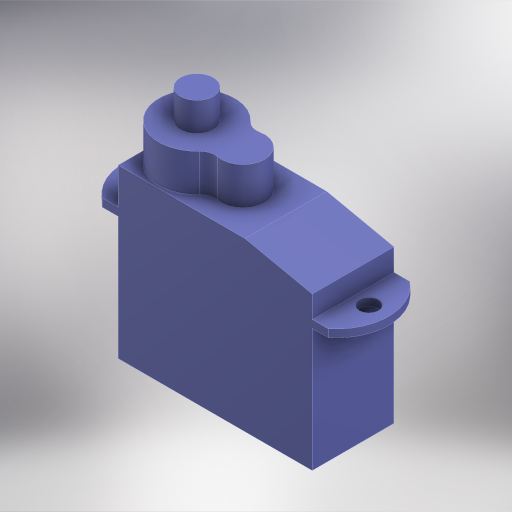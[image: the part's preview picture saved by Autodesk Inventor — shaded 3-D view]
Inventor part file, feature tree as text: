
AUTODESK INVENTOR PART (.ipt)
format: ipt  version: 2024 (Build 280153000, 153)  size: 352,768 bytes
history: native  units: in
note: dims shown in document units (in); Inventor stores cm internally (conversion verified against a paired STEP export)
features: chamfer x1, extrude x1, fillet x1, sketch x1
ambient origin geometry x8: Origin, YZ Plane, XZ Plane, XY Plane, X Axis, Y Axis, Z Axis, Center Point
bodies: Solid1 (feature_tree), Body1 (feature_tree)
feature tree (4):
  chamfer  "Chamfer1"  Distance=0.0591in Angle=45.0deg
  extrude  "Extrusion1"  Depth=0.0591in
  fillet  "Fillet1"  Radius=0.1969in
  sketch  "Sketch1"  dims[d3=0.1772in d4=0.4331in d5=0.1969in d6=0.0in d7=0.0591in]
